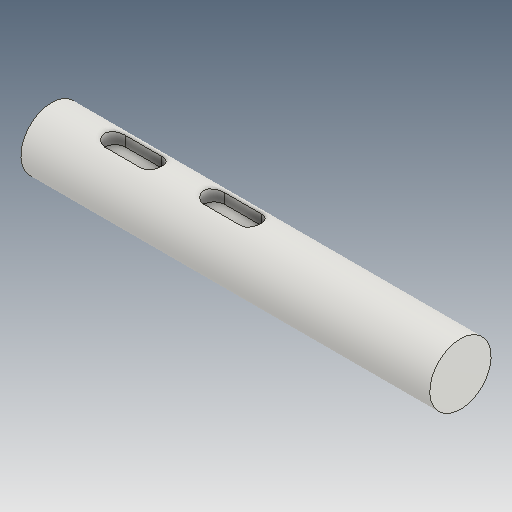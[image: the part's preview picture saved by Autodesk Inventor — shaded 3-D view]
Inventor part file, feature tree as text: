
AUTODESK INVENTOR PART (.ipt)
format: ipt  version: 2020.3 (Build 243373010, 373A)  size: 135,168 bytes
history: native  units: mm
features: other x7, revolve x1
ambient origin geometry x6: Origin, XZ Plane, XY Plane, X Axis, Y Axis, Z Axis
bodies: Solid1 (feature_tree)
feature tree (8):
  revolve  "Revolution1"  [1 undecoded]
  other  "Keyway1"
  other  "Keyway2"
  other  "Start Plane"
  other  "Origin point"
  other  "Main Sketch"
  other  "iFeature3:1"
  other  "iFeature3:2"
note: 1 required parameter value undecoded (feature->parameter linkage not recoverable at this tier; creation-order binding heuristic only, values carry confidence <= 0.55)
